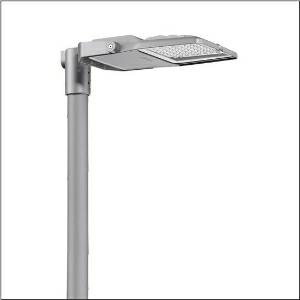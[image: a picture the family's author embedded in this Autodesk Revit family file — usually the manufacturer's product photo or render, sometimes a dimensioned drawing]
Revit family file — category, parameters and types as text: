
# Revit family: floodlight_fl_21_iq_mini___pl33t_5xa7772b4f3a_8cfb
name_source: partatom
category: Lighting Fixtures
units: mm (PartAtom-declared; Revit-internal decimal feet)

## family parameters
Cut with Voids When Loaded = No
Host = Face
Light Source = No
Part Type = Normal
Room Calculation Point = No
Round Connector Dimension = Use Diameter
Shared = No

## types (1)
- --- (1 x LED, 6420 lm, 45.5 W, 4000K)
    Apparent Load = 46 VA
    CIE Flux Codes = 26 75 99 100 100
    Color Rendering = 70
    Color Temperature = 4000K
    Default Elevation = 1800 mm
    Description = Floodlight FL 21 iQ mini, floodlight, primary light control with lens, of PMMA, primary optical cover: protective disc, of toughened safety glass, transparent, light distribution: PL33T, light emission: direct distribution, installation type: surface-mounted, lamps: LED, High Power LED, rated values: 6.420lm | 45,5W | 141,1lm/W (begin service life); end service life: 6.420lm | 48W; at 50% lumin. flux: 3.210lm | 21,5W | 149,3lm/W, colour temperature: 4000K, colour rendering: CRI > 70, light colour: 740, light setting 1 begin service life: 100% | 6.420lm | 45,5W | 141,1lm/W | 4.000K, light setting 1 end service life: 48W, further light settings possible, control: Street-Remote, Auto-Match, Temp-Guard, Night-Set, Smart-Wire, Desk-Remote (wireless, voltage-free reading and setting of iQ features in the workshop via application-optimized NFC function/RFID function), optimised constant luminous flux control (CLO 2.0), pre-setting: linear dimming characteristic, with terminal, 6-pole, mains connection: 220..240V, AC, 50/60Hz, luminaire housing, of diecast aluminium, powder-coated, SITECO metallic grey (DB 702S), corrosivity category C5 mid according to DIN EN ISO 12944suitable for swimming poolschlorine-resistant, sealing non-destructively replaceable, please order mast flange separately, mast bracket, of steel, galvanised, powder-coated, protection rating (complete): IP66, insulation class (complete): insulation class II (safety insulation), certification: CE, ENEC, VDE, protection symbol: D, impact resistance: IK08, permissible operating ambient temperature: -40..+40°C, permissible operating ambient temperature for outdoor applications: -40..+50°C, standard: DIN EN 12944, LABS conformity tested according to VDMA 24364:2018-05, packaging unit: 1 piece

Light Distribution: PL33T
    Height = 70 mm
    Lamp = 1 x LED
    Lamp Light Flux = 6420 lm
    Lamp Power = 45.5 W
    Lamp count = 1
    Length = 485 mm
    Luminous efficacy = 141 lm/W
    Manufacturer = Siteco
    ModVariant = No
    Model = 5XA7772B4F3A
    Number of Poles = 1
    OnlyDefault = Yes
    Power Factor = 1
    Product Name = Floodlight FL 21 iQ mini | PL33T
    Product group = floodlight | pylon annexe
    ProductGroupID = 6201
    Protection Class = Protection class II
    Protection Degree = IP 66
    RLX_Detail_Level = 1
    RLX_Emergency_Light_Flux = 0 lm
    RLX_Emergency_Type = 0
    RLX_Emergency_Type_DB = No
    RlxData = <blob elided: 101429 chars, md5=290b5cc5>
    Socket = socket
    Standby Power = 0 W
    System Light Flux = 6420 lm
    System Power = 46 W
    Type Comments = factory setting: luminous flux: 100 % | dim-lin: 254 | 463 mA
    Type Image = l_1007125.jpg
    URL = http://relux.com
    VarID = @adj_149383
    Voltage = 0 V
    Weight = 0.00 kg
    Width = 337 mm

## geometry (parser evidence)
native form markers: Blend x4, Sweep x12
no freeform markers — native parametric forms only
